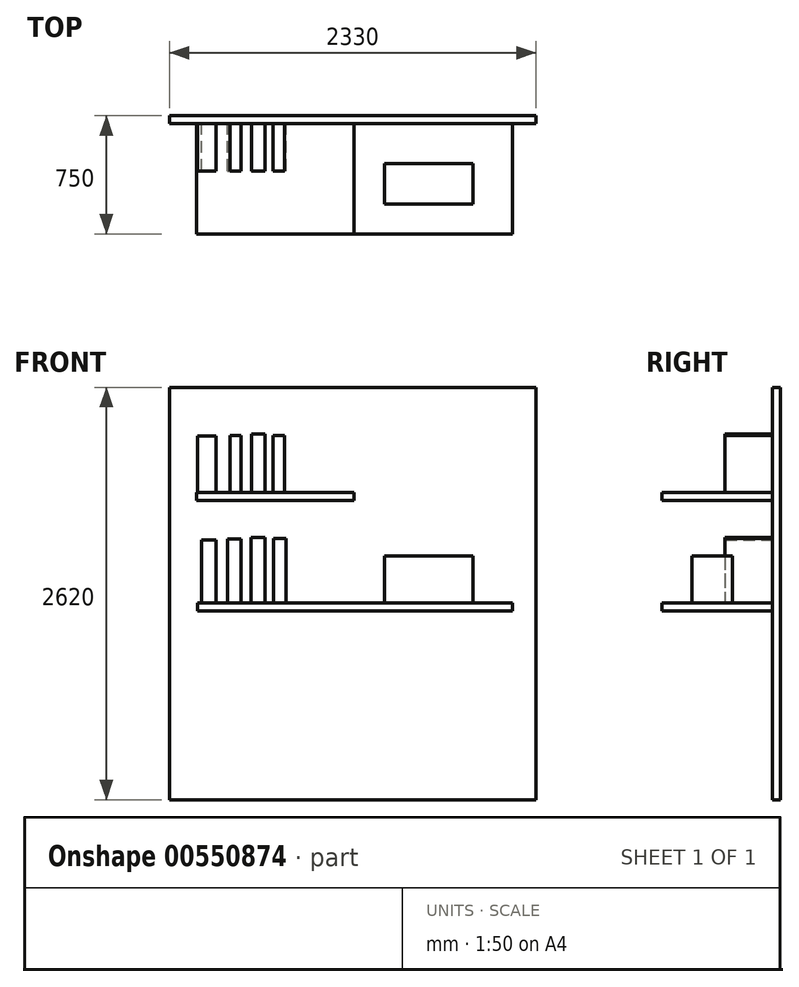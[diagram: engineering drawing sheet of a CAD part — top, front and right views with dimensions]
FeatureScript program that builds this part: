
annotation { "Feature Type Name" : "Feature", "Feature Type Description" : "" }
export const myFeature = defineFeature(function(context is Context, id is Id, definition is map)
    precondition{}
    {
        {
            var Q0;
            Q0=qCreatedBy(makeId("Front.planeOp"),FACE);
            var sketch = newSketch(context, id + "F0", { "sketchPlane" : qUnion([Q0])});
            skLineSegment(sketch, "E0.bottom", {"start": v(0, 0) * mm, "end": v(2330, 0) * mm});
            skLineSegment(sketch, "E0.top", {"start": v(0, 2620) * mm, "end": v(2330, 2620) * mm});
            skLineSegment(sketch, "E0.left", {"start": v(0, 0) * mm, "end": v(0, 2620) * mm});
            skLineSegment(sketch, "E0.right", {"start": v(2330, 0) * mm, "end": v(2330, 2620) * mm});
            skSolve(sketch);
        }
        {
            var Q0;
            Q0=makeQuery(id+"F0.imprint","IMPRINT",FACE,{"disambiguationData":[TD([[makeQuery(id+"F0.imprint","IMPRINT",EDGE,{"derivedFrom":sQuery(id+"F0.wireOp",EDGE,"E0.bottom")}),1.0]])]});
            extrude(context, id + "F1", {"entities" : qUnion([Q0]), "depth" : 50 * mm, "offsetDistance" : 25 * mm});
        }
        {
            var Q0;
            Q0=makeQuery(id+"F1.opExtrude","CAP_FACE",FACE,{"disambiguationData":[OSD([sQuery(id+"F0.wireOp",EDGE,"E0.bottom"),sQuery(id+"F0.wireOp",EDGE,"E0.top"),sQuery(id+"F0.wireOp",EDGE,"E0.left"),sQuery(id+"F0.wireOp",EDGE,"E0.right")])],"isStart":false});
            var sketch = newSketch(context, id + "F2", { "sketchPlane" : qUnion([Q0])});
            skLineSegment(sketch, "E1.bottom", {"start": v(180, 1250) * mm, "end": v(2180, 1250) * mm});
            skLineSegment(sketch, "E1.top", {"start": v(180, 1200) * mm, "end": v(2180, 1200) * mm});
            skLineSegment(sketch, "E1.left", {"start": v(180, 1250) * mm, "end": v(180, 1200) * mm});
            skLineSegment(sketch, "E1.right", {"start": v(2180, 1250) * mm, "end": v(2180, 1200) * mm});
            skSolve(sketch);
        }
        {
            var Q0;
            Q0 = qSketchRegion(id + "F2", true);
            extrude(context, id + "F3", {"entities" : qUnion([Q0]), "operationType" : NewBodyOperationType.ADD, "depth" : 700 * mm, "offsetDistance" : 25 * mm});
        }
        {
            var Q0;
            Q0=makeQuery(id+"F1.opExtrude","CAP_FACE",FACE,{"disambiguationData":[OSD([sQuery(id+"F0.wireOp",EDGE,"E0.bottom"),sQuery(id+"F0.wireOp",EDGE,"E0.top"),sQuery(id+"F0.wireOp",EDGE,"E0.left"),sQuery(id+"F0.wireOp",EDGE,"E0.right")])],"isStart":false});
            var sketch = newSketch(context, id + "F4", { "sketchPlane" : qUnion([Q0])});
            skLineSegment(sketch, "E2.bottom", {"start": v(172.87, 1950.93) * mm, "end": v(1172.87, 1950.93) * mm});
            skLineSegment(sketch, "E2.top", {"start": v(172.87, 1900.93) * mm, "end": v(1172.87, 1900.93) * mm});
            skLineSegment(sketch, "E2.left", {"start": v(172.87, 1950.93) * mm, "end": v(172.87, 1900.93) * mm});
            skLineSegment(sketch, "E2.right", {"start": v(1172.87, 1950.93) * mm, "end": v(1172.87, 1900.93) * mm});
            skSolve(sketch);
        }
        {
            var Q0;
            Q0 = qSketchRegion(id + "F4", true);
            extrude(context, id + "F5", {"entities" : qUnion([Q0]), "operationType" : NewBodyOperationType.ADD, "depth" : 700 * mm, "offsetDistance" : 25 * mm});
        }
        {
            var Q0;
            Q0=makeQuery(id+"F1.opExtrude","CAP_FACE",FACE,{"disambiguationData":[OSD([sQuery(id+"F0.wireOp",EDGE,"E0.bottom"),sQuery(id+"F0.wireOp",EDGE,"E0.top"),sQuery(id+"F0.wireOp",EDGE,"E0.left"),sQuery(id+"F0.wireOp",EDGE,"E0.right")])],"isStart":false});
            var sketch = newSketch(context, id + "F6", { "sketchPlane" : qUnion([Q0])});
            skLineSegment(sketch, "E3.bottom", {"start": v(205.51, 1649.34) * mm, "end": v(295.85, 1649.34) * mm});
            skLineSegment(sketch, "E3.top", {"start": v(205.51, 1250) * mm, "end": v(295.85, 1250) * mm});
            skLineSegment(sketch, "E3.left", {"start": v(205.51, 1649.34) * mm, "end": v(205.51, 1250) * mm});
            skLineSegment(sketch, "E3.right", {"start": v(295.85, 1649.34) * mm, "end": v(295.85, 1250) * mm});
            skLineSegment(sketch, "E4.bottom", {"start": v(368.05, 1656.18) * mm, "end": v(453.73, 1656.18) * mm});
            skLineSegment(sketch, "E4.top", {"start": v(368.05, 1250) * mm, "end": v(453.73, 1250) * mm});
            skLineSegment(sketch, "E4.left", {"start": v(368.05, 1656.18) * mm, "end": v(368.05, 1250) * mm});
            skLineSegment(sketch, "E4.right", {"start": v(453.73, 1656.18) * mm, "end": v(453.73, 1250) * mm});
            skLineSegment(sketch, "E5.bottom", {"start": v(520.16, 1666.73) * mm, "end": v(606.2, 1666.73) * mm});
            skLineSegment(sketch, "E5.top", {"start": v(520.16, 1250) * mm, "end": v(606.2, 1250) * mm});
            skLineSegment(sketch, "E5.left", {"start": v(520.16, 1666.73) * mm, "end": v(520.16, 1250) * mm});
            skLineSegment(sketch, "E5.right", {"start": v(606.2, 1666.73) * mm, "end": v(606.2, 1250) * mm});
            skLineSegment(sketch, "E6.bottom", {"start": v(661.07, 1658.7) * mm, "end": v(742.23, 1658.7) * mm});
            skLineSegment(sketch, "E6.top", {"start": v(661.07, 1250) * mm, "end": v(742.23, 1250) * mm});
            skLineSegment(sketch, "E6.left", {"start": v(661.07, 1658.7) * mm, "end": v(661.07, 1250) * mm});
            skLineSegment(sketch, "E6.right", {"start": v(742.23, 1658.7) * mm, "end": v(742.23, 1250) * mm});
            skLineSegment(sketch, "E7.bottom", {"start": v(180, 2311.1) * mm, "end": v(295.85, 2311.1) * mm});
            skLineSegment(sketch, "E7.top", {"start": v(180, 1950.93) * mm, "end": v(295.85, 1950.93) * mm});
            skLineSegment(sketch, "E7.left", {"start": v(180, 2311.1) * mm, "end": v(180, 1950.93) * mm});
            skLineSegment(sketch, "E7.right", {"start": v(295.85, 2311.1) * mm, "end": v(295.85, 1950.93) * mm});
            skLineSegment(sketch, "E8.bottom", {"start": v(384.73, 2312.69) * mm, "end": v(453.74, 2312.69) * mm});
            skLineSegment(sketch, "E8.top", {"start": v(384.73, 1950.93) * mm, "end": v(453.74, 1950.93) * mm});
            skLineSegment(sketch, "E8.left", {"start": v(384.73, 2312.69) * mm, "end": v(384.73, 1950.93) * mm});
            skLineSegment(sketch, "E8.right", {"start": v(453.74, 2312.69) * mm, "end": v(453.74, 1950.93) * mm});
            skLineSegment(sketch, "E9.bottom", {"start": v(522.19, 2323.11) * mm, "end": v(606.2, 2323.11) * mm});
            skLineSegment(sketch, "E9.top", {"start": v(522.19, 1950.93) * mm, "end": v(606.2, 1950.93) * mm});
            skLineSegment(sketch, "E9.left", {"start": v(522.19, 2323.11) * mm, "end": v(522.19, 1950.93) * mm});
            skLineSegment(sketch, "E9.right", {"start": v(606.2, 2323.11) * mm, "end": v(606.2, 1950.93) * mm});
            skLineSegment(sketch, "E10.bottom", {"start": v(658.21, 2315.04) * mm, "end": v(730.68, 2315.04) * mm});
            skLineSegment(sketch, "E10.top", {"start": v(658.21, 1950.93) * mm, "end": v(730.68, 1950.93) * mm});
            skLineSegment(sketch, "E10.left", {"start": v(658.21, 2315.04) * mm, "end": v(658.21, 1950.93) * mm});
            skLineSegment(sketch, "E10.right", {"start": v(730.68, 2315.04) * mm, "end": v(730.68, 1950.93) * mm});
            skSolve(sketch);
        }
        {
            var Q0;
            Q0 = qSketchRegion(id + "F6", true);
            extrude(context, id + "F7", {"entities" : qUnion([Q0]), "operationType" : NewBodyOperationType.ADD, "depth" : 300 * mm, "offsetDistance" : 25 * mm});
        }
        {
            var Q0;
            Q0=makeQuery(id+"F3.opExtrude","SWEPT_FACE",FACE,{"disambiguationData":[OSD([sQuery(id+"F2.wireOp",EDGE,"E1.bottom")])]});
            var sketch = newSketch(context, id + "F8", { "sketchPlane" : qUnion([Q0])});
            skLineSegment(sketch, "E11.bottom", {"start": v(1365.67, -305.07) * mm, "end": v(1929.9, -305.07) * mm});
            skLineSegment(sketch, "E11.top", {"start": v(1365.67, -559.94) * mm, "end": v(1929.9, -559.94) * mm});
            skLineSegment(sketch, "E11.left", {"start": v(1365.67, -305.07) * mm, "end": v(1365.67, -559.94) * mm});
            skLineSegment(sketch, "E11.right", {"start": v(1929.9, -305.07) * mm, "end": v(1929.9, -559.94) * mm});
            skSolve(sketch);
        }
        {
            var Q0;
            Q0=makeQuery(id+"F8.imprint","IMPRINT",FACE,{"disambiguationData":[TD([[makeQuery(id+"F8.imprint","IMPRINT",EDGE,{"derivedFrom":sQuery(id+"F8.wireOp",EDGE,"E11.bottom")}),-1.0]])]});
            extrude(context, id + "F9", {"entities" : qUnion([Q0]), "operationType" : NewBodyOperationType.ADD, "depth" : 300 * mm, "offsetDistance" : 25 * mm});
        }
    });
